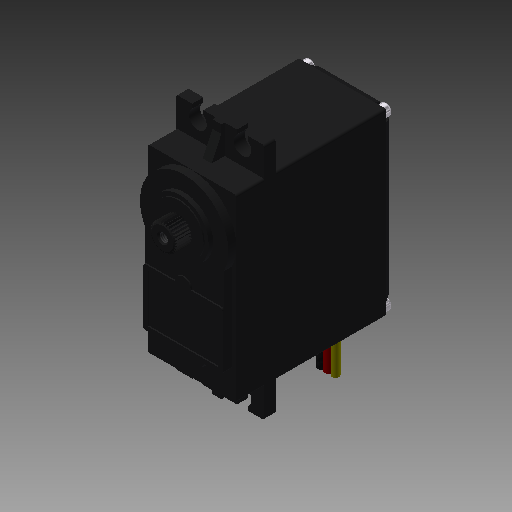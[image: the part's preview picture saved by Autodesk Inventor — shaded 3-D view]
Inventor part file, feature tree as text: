
AUTODESK INVENTOR PART (.ipt)
format: ipt  version: 2019 (Build 230136000, 136)  size: 732,672 bytes
history: native  units: mm
features: sketch x18, extrude x15, projected_geometry x5, fillet x4, chamfer x2, other x2, plane x1, mirror x1, pattern_circular x1, thread x1, revolve x1, pattern_linear x1
ambient origin geometry x8: Origin, YZ Plane, XZ Plane, XY Plane, X Axis, Y Axis, Z Axis, Center Point
bodies: Solid1 (feature_tree)
feature tree (52):
  extrude  "Extrusion1"  Depth=9.9mm
  extrude  "Extrusion2"  Depth=20.15mm
  fillet  "Fillet1"  Radius=35.25mm
  extrude  "Extrusion3"  Depth=10.0mm
  plane  "Work Plane1"
  extrude  "Extrusion4"  Depth=34.3mm
  extrude  "Extrusion5"  Depth=1.966646mm
  mirror  "Mirror1"
  extrude  "Extrusion6"  Depth=1.75mm TaperAngle=0.0deg
  extrude  "Extrusion7"  Depth=0.5mm
  extrude  "Extrusion8"  Depth=0.5mm
  extrude  "Extrusion9"  Depth=1.0mm
  pattern_circular  "Circular Pattern1"  [2 undecoded]
  extrude  "Extrusion10"  Depth=7.0mm
  chamfer  "Chamfer1"  Distance=2.5mm
  thread  "Thread1"  [1 undecoded]
  revolve  "Revolution1"  [1 undecoded]
  chamfer  "Chamfer2"  Distance=27.036082mm
  fillet  "Fillet2"  Radius=2.0mm
  extrude  "Extrusion11"  Depth=7.0mm
  extrude  "Extrusion12"  Depth=7.0mm TaperAngle=0.0deg
  fillet  "Fillet3"  Radius=11.2mm
  extrude  "Extrusion13"  Depth=7.0mm TaperAngle=0.0deg
  pattern_linear  "Rectangular Pattern1"  Spacing1=5.8mm  [1 undecoded]
  extrude  "Extrusion14"  Depth=7.0mm
  fillet  "Fillet4"  Radius=3.6mm
  extrude  "Extrusion15"  Depth=0.4mm
  other  "Decal1"
  sketch  "Sketch19"  dims[d32=2.5mm d33=1.25mm d34=24.15mm d35=2.5mm d36=0.0mm d37=1.85575mm d38=0.740982mm d39=27.036082mm d40=2.0mm d41=0.0mm d42=13.0mm d43=1.0mm d44=0.0mm d45=11.2mm d46=0.26mm d47=0.0mm d48=5.8mm d49=5.2mm d50=3.6mm d51=0.0mm d52=0.4mm d53=4.363323mm d54=3.6mm d55=0.0mm d56=300.0mm d57=360.0deg d59=0.189756mm d60=0.189756mm d61=1.9mm d62=3.0mm d63=0.0mm d64=0.3mm d65=2.0mm d66=45.0deg d67=10.0mm d68=0.0mm d69=90.0deg d70=1.0mm d71=2.0mm d72=60.0deg d73=0.5mm d74=3.6mm d75=8.6mm d76=18.8mm d77=1.7mm d78=0.0mm d79=1.5mm d80=0.0mm d81=0.5mm d82=0.2mm d83=0.2mm d84=0.9mm d85=0.9mm d86=0.7mm d87=0.0mm d88=20.0mm d90=17.1mm d91=20.0mm d93=37.6mm d94=4.0mm d95=6.0mm d96=3.0mm d97=1.0mm d98=7.0mm d99=-0.698132mm d100=0.5mm d101=1.6mm d102=1.6mm d103=1.6mm d104=1.6mm d105=1.6mm d106=7.0mm d107=0.0mm d118=40.3mm d119=53.3mm d120=2.5mm d121=4.9mm d122=2.0mm d123=19.8mm d124=4.0mm]
  sketch  "Sketch1"  dims[d0=19.8mm d1=9.9mm]
  sketch  "Sketch2"  dims[d2=40.3mm d3=20.15mm d4=35.25mm d5=0.0mm]
  sketch  "Sketch3"  dims[d6=10.0mm d7=17.75mm]
  sketch  "Sketch4"  dims[d8=8.875mm d9=34.3mm]
  sketch  "Sketch5"  dims[d10=4.8mm d11=1.966646mm]
  sketch  "Sketch6"  dims[d12=10.249769mm d13=1.75mm d14=0.0mm]
  sketch  "Sketch7"  dims[d15=0.5mm d16=12.8mm]
  sketch  "Sketch8"  dims[d17=0.5mm d18=3.6mm]
  sketch  "Sketch9"  dims[d19=1.0mm d20=1.0mm]
  sketch  "Sketch10"  dims[d21=1.0mm]
  sketch  "Sketch11"  dims[d22=1.0mm]
  sketch  "Sketch12"  dims[d23=0.3mm d24=0.0mm]
  sketch  "Sketch13"  dims[d25=-8.8mm]
  sketch  "Sketch14"  dims[d26=6.5mm d27=6.5mm]
  sketch  "Sketch15"  dims[d28=4.0mm]
  sketch  "Sketch16"  dims[d29=2.5mm]
  sketch  "Sketch17"  dims[d31=5.0mm]
  other  "Image1"
  projected_geometry  "Projected Loop9"
  projected_geometry  "Projected Loop10"
  projected_geometry  "Projected Loop11"
  projected_geometry  "Projected Loop12"
  projected_geometry  "Projected Loop13"
note: 5 required parameter values undecoded (feature->parameter linkage not recoverable at this tier; creation-order binding heuristic only, values carry confidence <= 0.55)